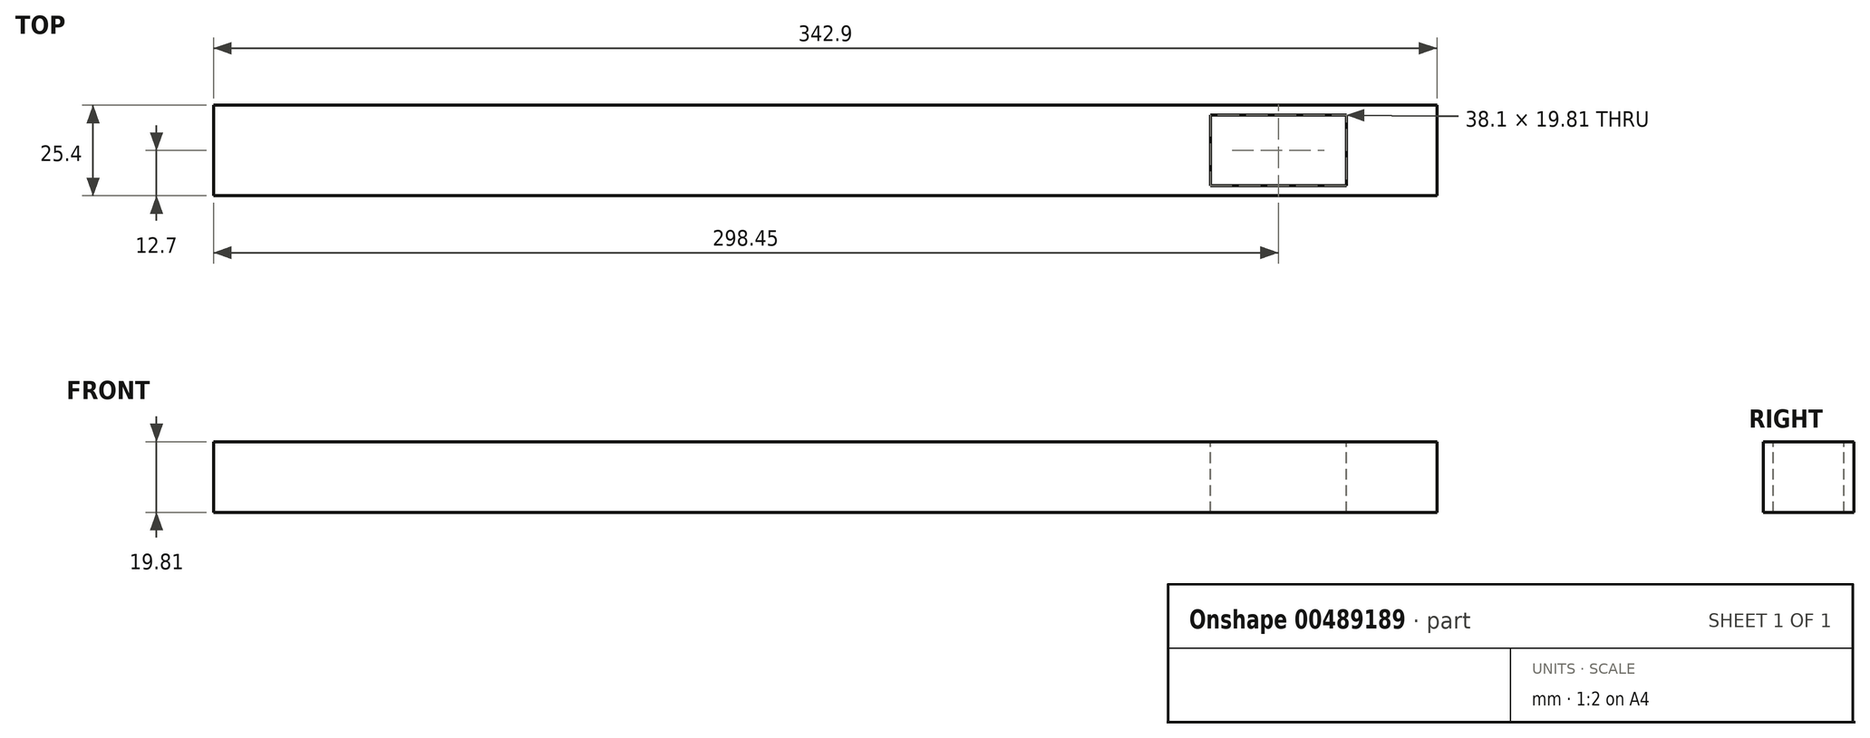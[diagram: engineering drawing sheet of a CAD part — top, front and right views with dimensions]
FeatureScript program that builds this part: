
annotation { "Feature Type Name" : "Feature", "Feature Type Description" : "" }
export const myFeature = defineFeature(function(context is Context, id is Id, definition is map)
    precondition{}
    {
        {
            var Q0;
            Q0=qCreatedBy(makeId("Front.planeOp"),FACE);
            var sketch = newSketch(context, id + "F0", { "sketchPlane" : qUnion([Q0])});
            skLineSegment(sketch, "E0.bottom", {"start": v(-254, 7.24) * mm, "end": v(88.9, 7.24) * mm});
            skLineSegment(sketch, "E0.top", {"start": v(-254, -12.57) * mm, "end": v(88.9, -12.57) * mm});
            skLineSegment(sketch, "E0.left", {"start": v(-254, 7.24) * mm, "end": v(-254, -12.57) * mm});
            skLineSegment(sketch, "E0.right", {"start": v(88.9, 7.24) * mm, "end": v(88.9, -12.57) * mm});
            skLineSegment(sketch, "E1", {"start": v(88.9, 7.24) * mm, "end": v(25.4, 7.24) * mm, "construction": true});
            skSolve(sketch);
        }
        {
            var Q0;
            Q0 = qSketchRegion(id + "F0", true);
            extrude(context, id + "F1", {"entities" : qUnion([Q0]), "depth" : 25.4 * mm, "offsetDistance" : 25.4 * mm});
        }
        {
            var Q0;
            Q0=makeQuery(id+"F1.opExtrude","SWEPT_FACE",FACE,{"disambiguationData":[OSD([sQuery(id+"F0.wireOp",EDGE,"E0.bottom")])]});
            var sketch = newSketch(context, id + "F2", { "sketchPlane" : qUnion([Q0])});
            skLineSegment(sketch, "E2.bottom", {"start": v(25.4, 0) * mm, "end": v(63.5, 0) * mm});
            skLineSegment(sketch, "E2.top", {"start": v(25.4, -25.4) * mm, "end": v(63.5, -25.4) * mm});
            skLineSegment(sketch, "E2.left", {"start": v(25.4, 0) * mm, "end": v(25.4, -25.4) * mm});
            skLineSegment(sketch, "E2.right", {"start": v(63.5, 0) * mm, "end": v(63.5, -25.4) * mm});
            skLineSegment(sketch, "E3.bottom", {"start": v(25.4, -2.8) * mm, "end": v(63.5, -2.8) * mm});
            skLineSegment(sketch, "E3.top", {"start": v(25.4, -22.6) * mm, "end": v(63.5, -22.6) * mm});
            skLineSegment(sketch, "E3.left", {"start": v(25.4, -2.8) * mm, "end": v(25.4, -22.6) * mm});
            skLineSegment(sketch, "E3.right", {"start": v(63.5, -2.8) * mm, "end": v(63.5, -22.6) * mm});
            skSolve(sketch);
        }
        {
            var Q0;
            Q0=makeQuery(id+"F2.imprint","IMPRINT",FACE,{"disambiguationData":[TD([[makeQuery(id+"F2.imprint","IMPRINT",EDGE,{"derivedFrom":sQuery(id+"F2.wireOp",EDGE,"E3.bottom")}),-1.0]])]});
            extrude(context, id + "F3", {"entities" : qUnion([Q0]), "operationType" : NewBodyOperationType.REMOVE, "oppositeDirection" : true, "depth" : 25.4 * mm, "offsetDistance" : 25.4 * mm});
        }
    });
